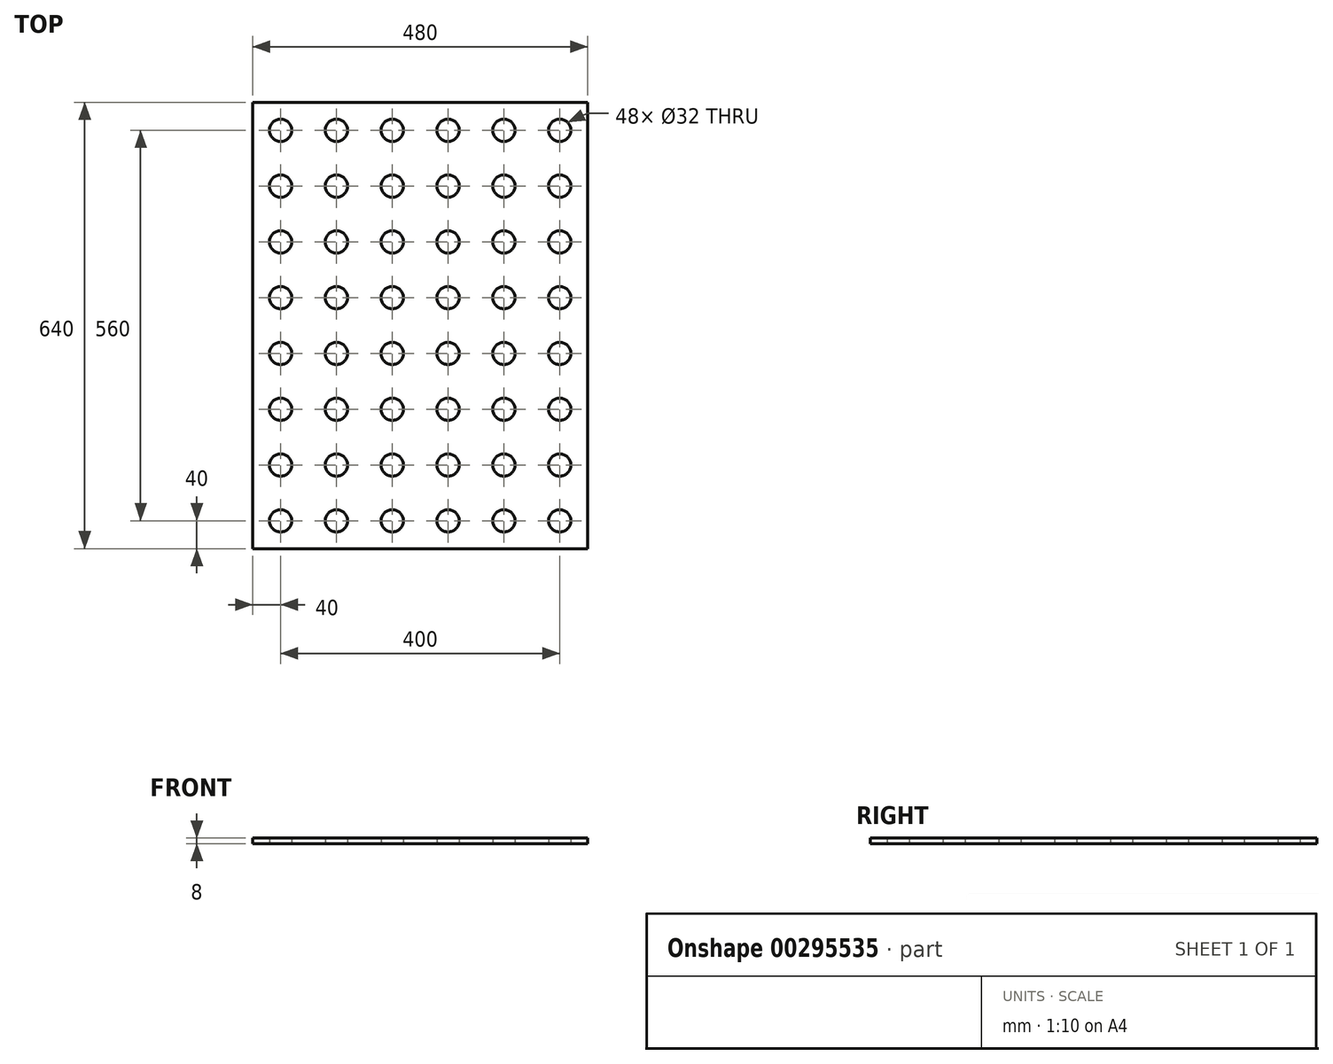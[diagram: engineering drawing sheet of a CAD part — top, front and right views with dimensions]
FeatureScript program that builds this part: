
annotation { "Feature Type Name" : "Feature", "Feature Type Description" : "" }
export const myFeature = defineFeature(function(context is Context, id is Id, definition is map)
    precondition{}
    {
        {
            var Q0;
            Q0=qCreatedBy(makeId("Top.planeOp"),FACE);
            var sketch = newSketch(context, id + "F0", { "sketchPlane" : qUnion([Q0])});
            skLineSegment(sketch, "E0.bottom", {"start": v(0, 0) * mm, "end": v(480, 0) * mm});
            skLineSegment(sketch, "E0.top", {"start": v(0, -640) * mm, "end": v(480, -640) * mm});
            skLineSegment(sketch, "E0.left", {"start": v(0, 0) * mm, "end": v(0, -640) * mm});
            skLineSegment(sketch, "E0.right", {"start": v(480, 0) * mm, "end": v(480, -640) * mm});
            skCircle(sketch, "E1", {"center": v(40, -40) * mm, "radius": 16 * mm});
            skCircle(sketch, "E2", {"center": v(40, -40) * mm, "radius": 40 * mm, "construction": true});
            skCircle(sketch, "E3.0.1.0", {"center": v(40, -120) * mm, "radius": 16 * mm});
            skCircle(sketch, "E3.0.1.1", {"center": v(40, -120) * mm, "radius": 40 * mm, "construction": true});
            skCircle(sketch, "E3.0.2.0", {"center": v(40, -200) * mm, "radius": 16 * mm});
            skCircle(sketch, "E3.0.2.1", {"center": v(40, -200) * mm, "radius": 40 * mm, "construction": true});
            skCircle(sketch, "E3.0.3.0", {"center": v(40, -280) * mm, "radius": 16 * mm});
            skCircle(sketch, "E3.0.3.1", {"center": v(40, -280) * mm, "radius": 40 * mm, "construction": true});
            skCircle(sketch, "E3.0.4.0", {"center": v(40, -360) * mm, "radius": 16 * mm});
            skCircle(sketch, "E3.0.4.1", {"center": v(40, -360) * mm, "radius": 40 * mm, "construction": true});
            skCircle(sketch, "E3.0.5.0", {"center": v(40, -440) * mm, "radius": 16 * mm});
            skCircle(sketch, "E3.0.5.1", {"center": v(40, -440) * mm, "radius": 40 * mm, "construction": true});
            skCircle(sketch, "E3.0.6.0", {"center": v(40, -520) * mm, "radius": 16 * mm});
            skCircle(sketch, "E3.0.6.1", {"center": v(40, -520) * mm, "radius": 40 * mm, "construction": true});
            skCircle(sketch, "E3.0.7.0", {"center": v(40, -600) * mm, "radius": 16 * mm});
            skCircle(sketch, "E3.0.7.1", {"center": v(40, -600) * mm, "radius": 40 * mm, "construction": true});
            skCircle(sketch, "E3.1.0.0", {"center": v(120, -40) * mm, "radius": 16 * mm});
            skCircle(sketch, "E3.1.0.1", {"center": v(120, -40) * mm, "radius": 40 * mm, "construction": true});
            skCircle(sketch, "E3.1.1.0", {"center": v(120, -120) * mm, "radius": 16 * mm});
            skCircle(sketch, "E3.1.1.1", {"center": v(120, -120) * mm, "radius": 40 * mm, "construction": true});
            skCircle(sketch, "E3.1.2.0", {"center": v(120, -200) * mm, "radius": 16 * mm});
            skCircle(sketch, "E3.1.2.1", {"center": v(120, -200) * mm, "radius": 40 * mm, "construction": true});
            skCircle(sketch, "E3.1.3.0", {"center": v(120, -280) * mm, "radius": 16 * mm});
            skCircle(sketch, "E3.1.3.1", {"center": v(120, -280) * mm, "radius": 40 * mm, "construction": true});
            skCircle(sketch, "E3.1.4.0", {"center": v(120, -360) * mm, "radius": 16 * mm});
            skCircle(sketch, "E3.1.4.1", {"center": v(120, -360) * mm, "radius": 40 * mm, "construction": true});
            skCircle(sketch, "E3.1.5.0", {"center": v(120, -440) * mm, "radius": 16 * mm});
            skCircle(sketch, "E3.1.5.1", {"center": v(120, -440) * mm, "radius": 40 * mm, "construction": true});
            skCircle(sketch, "E3.1.6.0", {"center": v(120, -520) * mm, "radius": 16 * mm});
            skCircle(sketch, "E3.1.6.1", {"center": v(120, -520) * mm, "radius": 40 * mm, "construction": true});
            skCircle(sketch, "E3.1.7.0", {"center": v(120, -600) * mm, "radius": 16 * mm});
            skCircle(sketch, "E3.1.7.1", {"center": v(120, -600) * mm, "radius": 40 * mm, "construction": true});
            skCircle(sketch, "E3.2.0.0", {"center": v(200, -40) * mm, "radius": 16 * mm});
            skCircle(sketch, "E3.2.0.1", {"center": v(200, -40) * mm, "radius": 40 * mm, "construction": true});
            skCircle(sketch, "E3.2.1.0", {"center": v(200, -120) * mm, "radius": 16 * mm});
            skCircle(sketch, "E3.2.1.1", {"center": v(200, -120) * mm, "radius": 40 * mm, "construction": true});
            skCircle(sketch, "E3.2.2.0", {"center": v(200, -200) * mm, "radius": 16 * mm});
            skCircle(sketch, "E3.2.2.1", {"center": v(200, -200) * mm, "radius": 40 * mm, "construction": true});
            skCircle(sketch, "E3.2.3.0", {"center": v(200, -280) * mm, "radius": 16 * mm});
            skCircle(sketch, "E3.2.3.1", {"center": v(200, -280) * mm, "radius": 40 * mm, "construction": true});
            skCircle(sketch, "E3.2.4.0", {"center": v(200, -360) * mm, "radius": 16 * mm});
            skCircle(sketch, "E3.2.4.1", {"center": v(200, -360) * mm, "radius": 40 * mm, "construction": true});
            skCircle(sketch, "E3.2.5.0", {"center": v(200, -440) * mm, "radius": 16 * mm});
            skCircle(sketch, "E3.2.5.1", {"center": v(200, -440) * mm, "radius": 40 * mm, "construction": true});
            skCircle(sketch, "E3.2.6.0", {"center": v(200, -520) * mm, "radius": 16 * mm});
            skCircle(sketch, "E3.2.6.1", {"center": v(200, -520) * mm, "radius": 40 * mm, "construction": true});
            skCircle(sketch, "E3.2.7.0", {"center": v(200, -600) * mm, "radius": 16 * mm});
            skCircle(sketch, "E3.2.7.1", {"center": v(200, -600) * mm, "radius": 40 * mm, "construction": true});
            skCircle(sketch, "E3.3.0.0", {"center": v(280, -40) * mm, "radius": 16 * mm});
            skCircle(sketch, "E3.3.0.1", {"center": v(280, -40) * mm, "radius": 40 * mm, "construction": true});
            skCircle(sketch, "E3.3.1.0", {"center": v(280, -120) * mm, "radius": 16 * mm});
            skCircle(sketch, "E3.3.1.1", {"center": v(280, -120) * mm, "radius": 40 * mm, "construction": true});
            skCircle(sketch, "E3.3.2.0", {"center": v(280, -200) * mm, "radius": 16 * mm});
            skCircle(sketch, "E3.3.2.1", {"center": v(280, -200) * mm, "radius": 40 * mm, "construction": true});
            skCircle(sketch, "E3.3.3.0", {"center": v(280, -280) * mm, "radius": 16 * mm});
            skCircle(sketch, "E3.3.3.1", {"center": v(280, -280) * mm, "radius": 40 * mm, "construction": true});
            skCircle(sketch, "E3.3.4.0", {"center": v(280, -360) * mm, "radius": 16 * mm});
            skCircle(sketch, "E3.3.4.1", {"center": v(280, -360) * mm, "radius": 40 * mm, "construction": true});
            skCircle(sketch, "E3.3.5.0", {"center": v(280, -440) * mm, "radius": 16 * mm});
            skCircle(sketch, "E3.3.5.1", {"center": v(280, -440) * mm, "radius": 40 * mm, "construction": true});
            skCircle(sketch, "E3.3.6.0", {"center": v(280, -520) * mm, "radius": 16 * mm});
            skCircle(sketch, "E3.3.6.1", {"center": v(280, -520) * mm, "radius": 40 * mm, "construction": true});
            skCircle(sketch, "E3.3.7.0", {"center": v(280, -600) * mm, "radius": 16 * mm});
            skCircle(sketch, "E3.3.7.1", {"center": v(280, -600) * mm, "radius": 40 * mm, "construction": true});
            skCircle(sketch, "E3.4.0.0", {"center": v(360, -40) * mm, "radius": 16 * mm});
            skCircle(sketch, "E3.4.0.1", {"center": v(360, -40) * mm, "radius": 40 * mm, "construction": true});
            skCircle(sketch, "E3.4.1.0", {"center": v(360, -120) * mm, "radius": 16 * mm});
            skCircle(sketch, "E3.4.1.1", {"center": v(360, -120) * mm, "radius": 40 * mm, "construction": true});
            skCircle(sketch, "E3.4.2.0", {"center": v(360, -200) * mm, "radius": 16 * mm});
            skCircle(sketch, "E3.4.2.1", {"center": v(360, -200) * mm, "radius": 40 * mm, "construction": true});
            skCircle(sketch, "E3.4.3.0", {"center": v(360, -280) * mm, "radius": 16 * mm});
            skCircle(sketch, "E3.4.3.1", {"center": v(360, -280) * mm, "radius": 40 * mm, "construction": true});
            skCircle(sketch, "E3.4.4.0", {"center": v(360, -360) * mm, "radius": 16 * mm});
            skCircle(sketch, "E3.4.4.1", {"center": v(360, -360) * mm, "radius": 40 * mm, "construction": true});
            skCircle(sketch, "E3.4.5.0", {"center": v(360, -440) * mm, "radius": 16 * mm});
            skCircle(sketch, "E3.4.5.1", {"center": v(360, -440) * mm, "radius": 40 * mm, "construction": true});
            skCircle(sketch, "E3.4.6.0", {"center": v(360, -520) * mm, "radius": 16 * mm});
            skCircle(sketch, "E3.4.6.1", {"center": v(360, -520) * mm, "radius": 40 * mm, "construction": true});
            skCircle(sketch, "E3.4.7.0", {"center": v(360, -600) * mm, "radius": 16 * mm});
            skCircle(sketch, "E3.4.7.1", {"center": v(360, -600) * mm, "radius": 40 * mm, "construction": true});
            skCircle(sketch, "E3.5.0.0", {"center": v(440, -40) * mm, "radius": 16 * mm});
            skCircle(sketch, "E3.5.0.1", {"center": v(440, -40) * mm, "radius": 40 * mm, "construction": true});
            skCircle(sketch, "E3.5.1.0", {"center": v(440, -120) * mm, "radius": 16 * mm});
            skCircle(sketch, "E3.5.1.1", {"center": v(440, -120) * mm, "radius": 40 * mm, "construction": true});
            skCircle(sketch, "E3.5.2.0", {"center": v(440, -200) * mm, "radius": 16 * mm});
            skCircle(sketch, "E3.5.2.1", {"center": v(440, -200) * mm, "radius": 40 * mm, "construction": true});
            skCircle(sketch, "E3.5.3.0", {"center": v(440, -280) * mm, "radius": 16 * mm});
            skCircle(sketch, "E3.5.3.1", {"center": v(440, -280) * mm, "radius": 40 * mm, "construction": true});
            skCircle(sketch, "E3.5.4.0", {"center": v(440, -360) * mm, "radius": 16 * mm});
            skCircle(sketch, "E3.5.4.1", {"center": v(440, -360) * mm, "radius": 40 * mm, "construction": true});
            skCircle(sketch, "E3.5.5.0", {"center": v(440, -440) * mm, "radius": 16 * mm});
            skCircle(sketch, "E3.5.5.1", {"center": v(440, -440) * mm, "radius": 40 * mm, "construction": true});
            skCircle(sketch, "E3.5.6.0", {"center": v(440, -520) * mm, "radius": 16 * mm});
            skCircle(sketch, "E3.5.6.1", {"center": v(440, -520) * mm, "radius": 40 * mm, "construction": true});
            skCircle(sketch, "E3.5.7.0", {"center": v(440, -600) * mm, "radius": 16 * mm});
            skCircle(sketch, "E3.5.7.1", {"center": v(440, -600) * mm, "radius": 40 * mm, "construction": true});
            skLineSegment(sketch, "E3.direction1", {"start": v(40, -40) * mm, "end": v(120, -40) * mm, "construction": true});
            skLineSegment(sketch, "E3.direction2", {"start": v(40, -40) * mm, "end": v(40, -120) * mm, "construction": true});
            skSolve(sketch);
        }
        {
            var Q0;
            Q0=makeQuery(id+"F0.imprint","IMPRINT",FACE,{"disambiguationData":[TD([[makeQuery(id+"F0.imprint","IMPRINT",EDGE,{"derivedFrom":sQuery(id+"F0.wireOp",EDGE,"E0.bottom")}),-1.0]])]});
            extrude(context, id + "F1", {"entities" : qUnion([Q0]), "depth" : 8 * mm});
        }
    });
